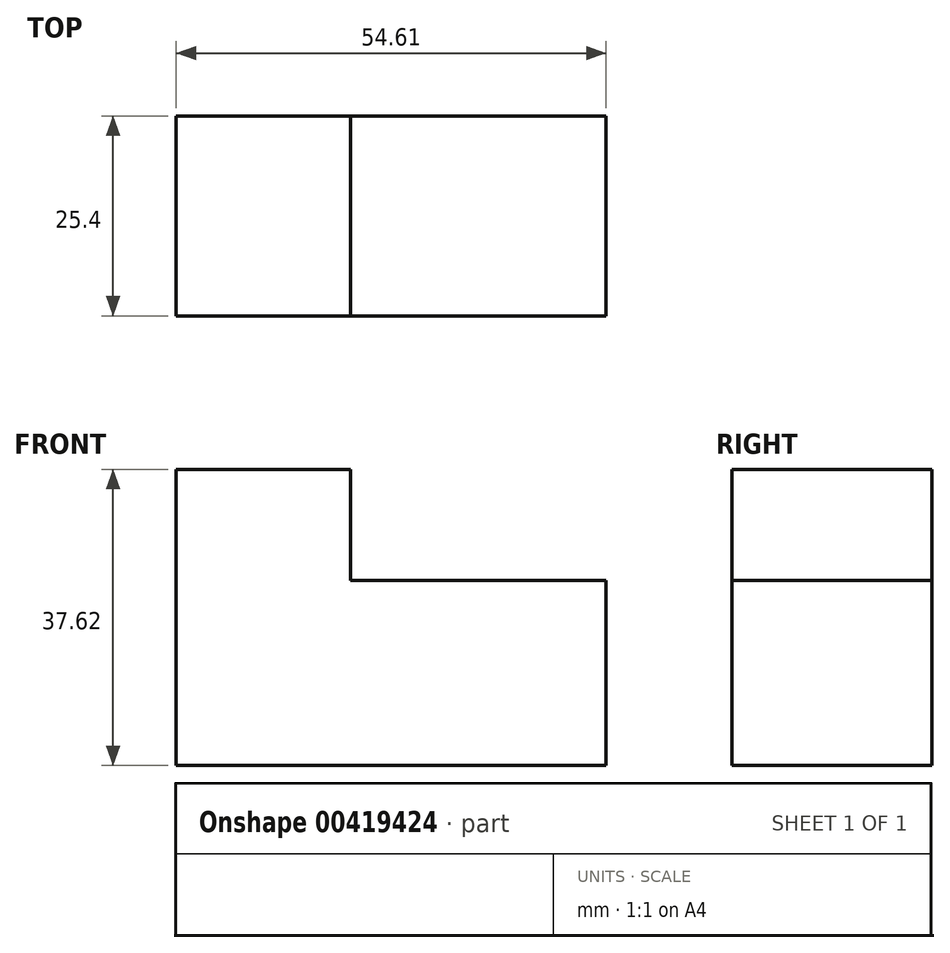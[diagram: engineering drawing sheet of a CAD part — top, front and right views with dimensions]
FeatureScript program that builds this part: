
annotation { "Feature Type Name" : "Feature", "Feature Type Description" : "" }
export const myFeature = defineFeature(function(context is Context, id is Id, definition is map)
    precondition{}
    {
        {
            var Q0;
            Q0=qCreatedBy(makeId("Front.planeOp"),FACE);
            var sketch = newSketch(context, id + "F0", { "sketchPlane" : qUnion([Q0])});
            skLineSegment(sketch, "E0", {"start": v(0, 0) * mm, "end": v(-54.61, 0) * mm});
            skLineSegment(sketch, "E1", {"start": v(-54.61, 0) * mm, "end": v(-54.61, 37.62) * mm});
            skLineSegment(sketch, "E2", {"start": v(-54.61, 37.62) * mm, "end": v(-32.46, 37.62) * mm});
            skLineSegment(sketch, "E3", {"start": v(-32.46, 37.62) * mm, "end": v(-32.46, 23.49) * mm});
            skLineSegment(sketch, "E4", {"start": v(-32.46, 23.49) * mm, "end": v(0, 23.49) * mm});
            skLineSegment(sketch, "E5", {"start": v(0, 23.49) * mm, "end": v(0, 0) * mm});
            skSolve(sketch);
        }
        {
            var Q0;
            Q0 = qSketchRegion(id + "F0", true);
            extrude(context, id + "F1", {"entities" : qUnion([Q0]), "depth" : 25.4 * mm});
        }
    });
